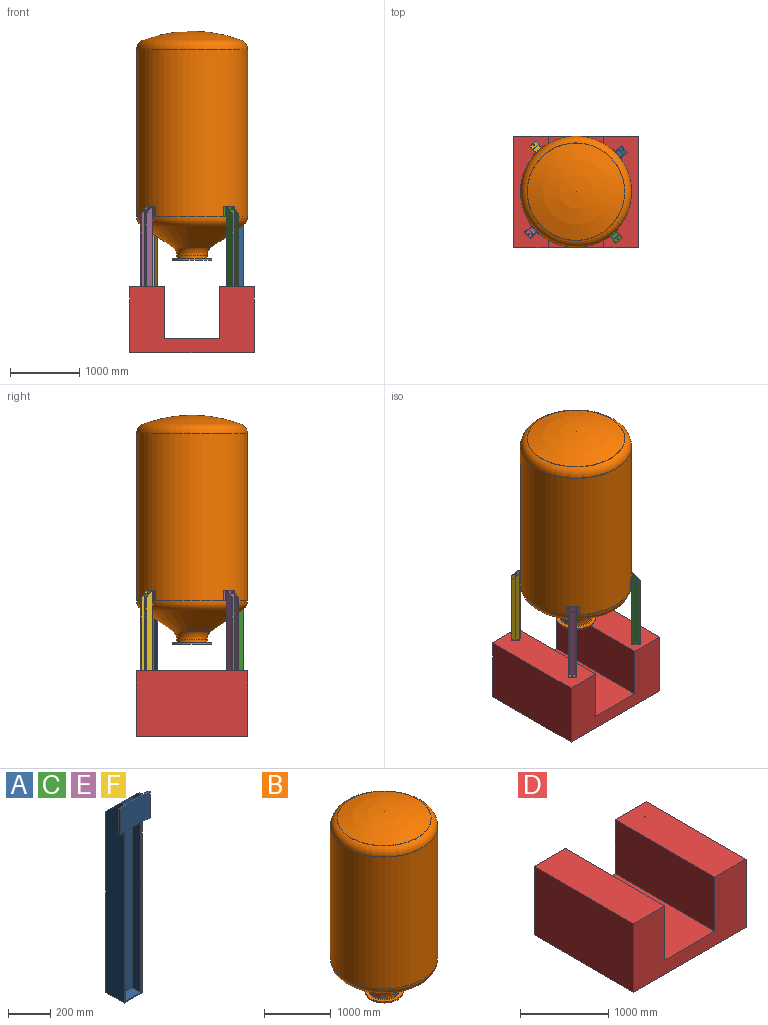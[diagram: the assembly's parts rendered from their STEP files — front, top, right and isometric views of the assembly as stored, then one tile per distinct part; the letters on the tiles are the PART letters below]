
ASSEMBLY  parts=6 mates=5
PART A: 29 faces, bbox 202.5x139x1156 mm
  f0: plane 1156x125mm, normal (-1,0,0), area 138293.1mm2, adj f1,f2,f9,f10,f19,f22,f23,f25
  f1: plane 1051x120mm, normal (0,1,0), area 21620mm2, adj f0,f15,f17,f18,f19,f21,f23
  f2: plane 202.5x34.05mm, normal (0,0,1), area 2431.9mm2, adj f0,f3,f4,f5,f6,f7,f8,f12
  f3: cylinder r=810mm len=150mm, axis (0,0,-1), area 13424mm2, adj f2,f9,f24,f26
  f4: cylinder r=810mm len=150mm, axis (0,0,-1), area 5526.8mm2, adj f2,f7,f9,f27
  f5: plane 150x9.92mm, normal (-0.99,-0.12,0), area 1500mm2, adj f2,f6,f8,f9
  f6: cylinder r=800mm len=200mm, axis (0,0,-1), area 30078.7mm2, adj f2,f5,f7,f9
  f7: plane 150x9.92mm, normal (0.99,-0.13,0), area 1500mm2, adj f2,f4,f6,f9
  f8: cylinder r=810mm len=150mm, axis (0,0,-1), area 5526.8mm2, adj f2,f5,f9,f25
  f9: plane 202.5x20.03mm, normal (0,0,-1), area 2039mm2, adj f0,f3,f4,f5,f6,f7,f8,f10
  f10: cylinder r=810mm len=1000mm, axis (0,0,1), area 10023.2mm2, adj f0,f9,f14,f20
  f11: cylinder r=810mm len=1000mm, axis (0,0,1), area 10023.2mm2, adj f9,f12,f18,f20
  f12: plane 1150x56.82mm, normal (-1,0,0), area 63844mm2, adj f2,f9,f11,f13,f19,f20,f26
  f13: plane 1112.5x100mm, normal (0,-1,0), area 111250mm2, adj f12,f14,f19,f20
  f14: plane 1150x56.82mm, normal (1,0,0), area 63844mm2, adj f2,f9,f10,f13,f19,f20,f24
  f15: plane 1102.5x57.5mm, normal (1,0,0), area 61740.6mm2, adj f1,f16,f19,f21
  f16: plane 1102.5x100mm, normal (0,1,0), area 110250mm2, adj f15,f17,f19,f21
  f17: plane 1102.5x57.5mm, normal (-1,0,0), area 61740.6mm2, adj f1,f16,f19,f21
  f18: plane 1156x125mm, normal (1,0,0), area 138293.1mm2, adj f1,f2,f9,f11,f19,f22,f23,f27
  f19: plane 120x105mm, normal (0,0.71,0.71), area 4384.1mm2, adj f0,f1,f2,f12,f13,f14,f15,f16
  f20: plane 120x57.5mm, normal (0,0,1), area 5757mm2, adj f10,f11,f12,f13,f14,f22
  f21: plane 100x57.5mm, normal (0,0,1), area 5617.3mm2, adj f1,f15,f16,f17,f28
  f22: plane 120x6mm, normal (0,-1,0), area 720mm2, adj f0,f18,f20,f23
  f23: plane 125x120mm, normal (0,0,-1), area 14867.3mm2, adj f0,f1,f18,f22,f28
  f24: cylinder r=5mm len=150mm, axis (0,0,-1), area 1219.5mm2, adj f2,f3,f9,f14
  f25: cylinder r=5mm len=150mm, axis (0,0,-1), area 1118.2mm2, adj f0,f2,f8,f9
  f26: cylinder r=5mm len=150mm, axis (0,0,-1), area 1219.5mm2, adj f2,f3,f9,f12
  f27: cylinder r=5mm len=150mm, axis (0,0,-1), area 1118.2mm2, adj f2,f4,f9,f18
  f28: cylinder r=6.5mm len=13mm, axis (0,0,1), area 245mm2, adj f21,f23
PART B: 18 faces, bbox 1731.8x1731.8x3340.6 mm
  f0: cylinder r=285mm len=570mm, axis (0,0,1), area 35814.2mm2, adj f1,f9
  f1: plane 570x570mm, normal (0,0,-1), area 114645.4mm2, adj f0,f16
  f2: sphere r=2000mm, area 1602371.1mm2, adj f3
  f3: torus R=650mm, axis (0,0,1), area 874708.9mm2, adj f2,f4
  f4: cylinder r=800mm len=2407.53mm, axis (0,0,1), area 12101542.3mm2, adj f3,f5
  f5: torus R=650mm, axis (0,0,1), area 713930.7mm2, adj f4,f6
  f6: cone r=734.24mm half-angle=55.8deg, axis (0,0,1), area 1741270.2mm2, adj f5,f7
  f7: torus R=368mm, axis (0,0,1), area 221001.2mm2, adj f6,f8
  f8: cylinder r=218mm len=436mm, axis (0,0,1), area 55508.9mm2, adj f7,f17
  f9: plane 570x570mm, normal (0,0,1), area 91863.3mm2, adj f0,f17
  f10: sphere r=1993.5mm, area 1591972.6mm2, adj f11
  f11: torus R=650mm, axis (0,0,1), area 831317.9mm2, adj f10,f12
  f12: cylinder r=793.5mm len=2407.53mm, axis (0,0,1), area 12003217.2mm2, adj f11,f13
  f13: torus R=650mm, axis (0,0,1), area 678144.6mm2, adj f12,f14
  f14: cone r=730.59mm half-angle=55.8deg, axis (0,0,1), area 1728781.8mm2, adj f13,f15
  f15: torus R=368mm, axis (0,0,1), area 225289.6mm2, adj f14,f16
  f16: cylinder r=211.5mm len=423mm, axis (0,0,1), area 93720.7mm2, adj f1,f15
  f17: torus R=228mm, axis (0,0,1), area 21874.4mm2, adj f8,f9
PART C: same geometry as A
PART D: 13 faces, bbox 1800x1600x950 mm
  f0: plane 1600x800mm, normal (0,0,1), area 1120956.9mm2, adj f1,f3,f6,f8,f10
  f1: plane 1800x950mm, normal (0,1,0), area 1110000mm2, adj f0,f2,f4,f5,f6,f7,f8,f9
  f2: plane 1600x950mm, normal (-1,0,0), area 1520000mm2, adj f1,f3,f5,f7
  f3: plane 1800x950mm, normal (0,-1,0), area 1110000mm2, adj f0,f2,f4,f5,f6,f7,f8,f9
  f4: plane 1600x950mm, normal (1,0,0), area 1520000mm2, adj f1,f3,f5,f9
  f5: plane 1800x1600mm, normal (0,0,-1), area 2720956.9mm2, adj f1,f2,f3,f4,f10
  f6: plane 1600x750mm, normal (1,0,0), area 1200000mm2, adj f0,f1,f3,f7
  f7: plane 1600x500mm, normal (0,0,1), area 800000mm2, adj f1,f2,f3,f6
  f8: plane 1600x750mm, normal (-1,0,0), area 1200000mm2, adj f0,f1,f3,f9
  f9: plane 1600x500mm, normal (0,0,1), area 799867.3mm2, adj f1,f3,f4,f8,f11
  f10: cylinder r=225mm len=450mm, axis (0,0,1), area 282743.3mm2, adj f0,f5
  f11: cylinder r=6.5mm len=25mm, axis (0,0,1), area 1021mm2, adj f9,f12
  f12: plane 13x13mm, normal (0,0,1), area 132.7mm2, adj f11
PART E: same geometry as A
PART F: same geometry as A
PLACE A rot(axis=(0,0,-1),48.4deg) t=(900,-800,1956)mm
PLACE B t=(900,-800,1331.47)mm
PLACE C rot(axis=(0,0,-1),138.4deg) t=(900,-800,1956)mm
PLACE D at identity fixed
PLACE E rot(axis=(0,0,1),131.6deg) t=(900,-800,1956)mm
PLACE F rot(axis=(0,0,1),41.6deg) t=(900,-800,1956)mm
MATE cylindrical D.f11 <-> A.f28  axis (0,0,1) through (1578.27,-197.09,937.5)mm
MATE slider D.f10 <-> B.f6  axis (0,0,1) through (900,-800,100)mm
MATE planar D.f9 <-> A.f23  axis (0,0,1) through (1550,-800.1,950)mm
MATE cylindrical B.f3 <-> A.f3  axis (0,0,1) through (900,-800,4448.95)mm
MATE planar A.f9 <-> B.f6  axis (0,0,-1) through (1460.55,-215.3,1956)mm
